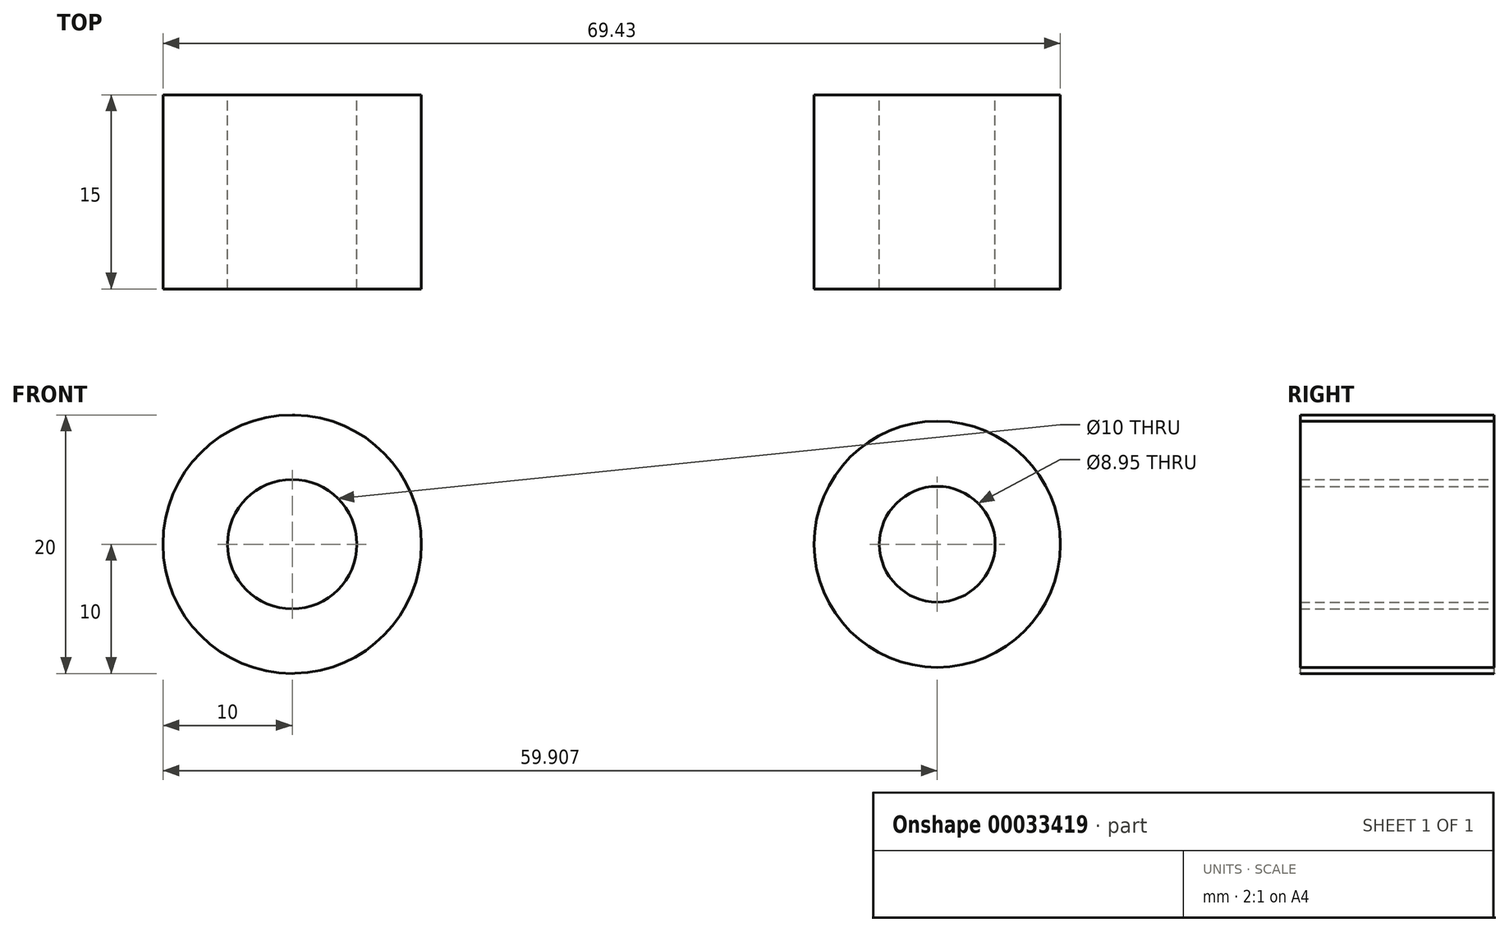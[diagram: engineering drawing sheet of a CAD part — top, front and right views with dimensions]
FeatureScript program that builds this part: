
annotation { "Feature Type Name" : "Feature", "Feature Type Description" : "" }
export const myFeature = defineFeature(function(context is Context, id is Id, definition is map)
    precondition{}
    {
        {
            var Q0;
            Q0=qCreatedBy(makeId("Front.planeOp"),FACE);
            var sketch = newSketch(context, id + "F0", { "sketchPlane" : qUnion([Q0])});
            skCircle(sketch, "E0", {"center": v(0, 0) * mm, "radius": 5 * mm});
            skCircle(sketch, "E1", {"center": v(0, 0) * mm, "radius": 10 * mm});
            skCircle(sketch, "E2", {"center": v(49.9, 0) * mm, "radius": 4.48 * mm});
            skCircle(sketch, "E3", {"center": v(49.9, 0) * mm, "radius": 9.52 * mm});
            skLineSegment(sketch, "E4", {"start": v(0, 10) * mm, "end": v(50, 9.52) * mm});
            skLineSegment(sketch, "E5", {"start": v(0, -10) * mm, "end": v(50, -9.52) * mm});
            skSolve(sketch);
        }
        {
            var Q0;
            {var subQ1=sQuery(id+"F0.wireOp",EDGE,"E1");var subQ5=sQuery(id+"F0.wireOp",EDGE,"E4");var subQ6=makeQuery(id+"F0.imprint","INTERSECT",VERTEX,{"disambiguationData":[OD(1.0)],"derivedFrom":[subQ1,subQ5]});Q0=makeQuery(id+"F0.imprint","IMPRINT",FACE,{"disambiguationData":[TD([[makeQuery(id+"F0.imprint","IMPRINT",EDGE,{"disambiguationData":[TD([[subQ6,1.0]])],"derivedFrom":subQ1}),-1.0]])]});}
            var Q1;
            Q1=makeQuery(id+"F0.imprint","IMPRINT",FACE,{"disambiguationData":[TD([[makeQuery(id+"F0.imprint","IMPRINT",EDGE,{"derivedFrom":sQuery(id+"F0.wireOp",EDGE,"E0")}),-1.0]])]});
            var Q2;
            Q2=makeQuery(id+"F0.imprint","IMPRINT",FACE,{"disambiguationData":[TD([[makeQuery(id+"F0.imprint","IMPRINT",EDGE,{"derivedFrom":sQuery(id+"F0.wireOp",EDGE,"E2")}),-1.0]])]});
            extrude(context, id + "F1", {"entities" : qUnion([Q0, Q1, Q2]), "depth" : 15 * mm});
        }
    });
